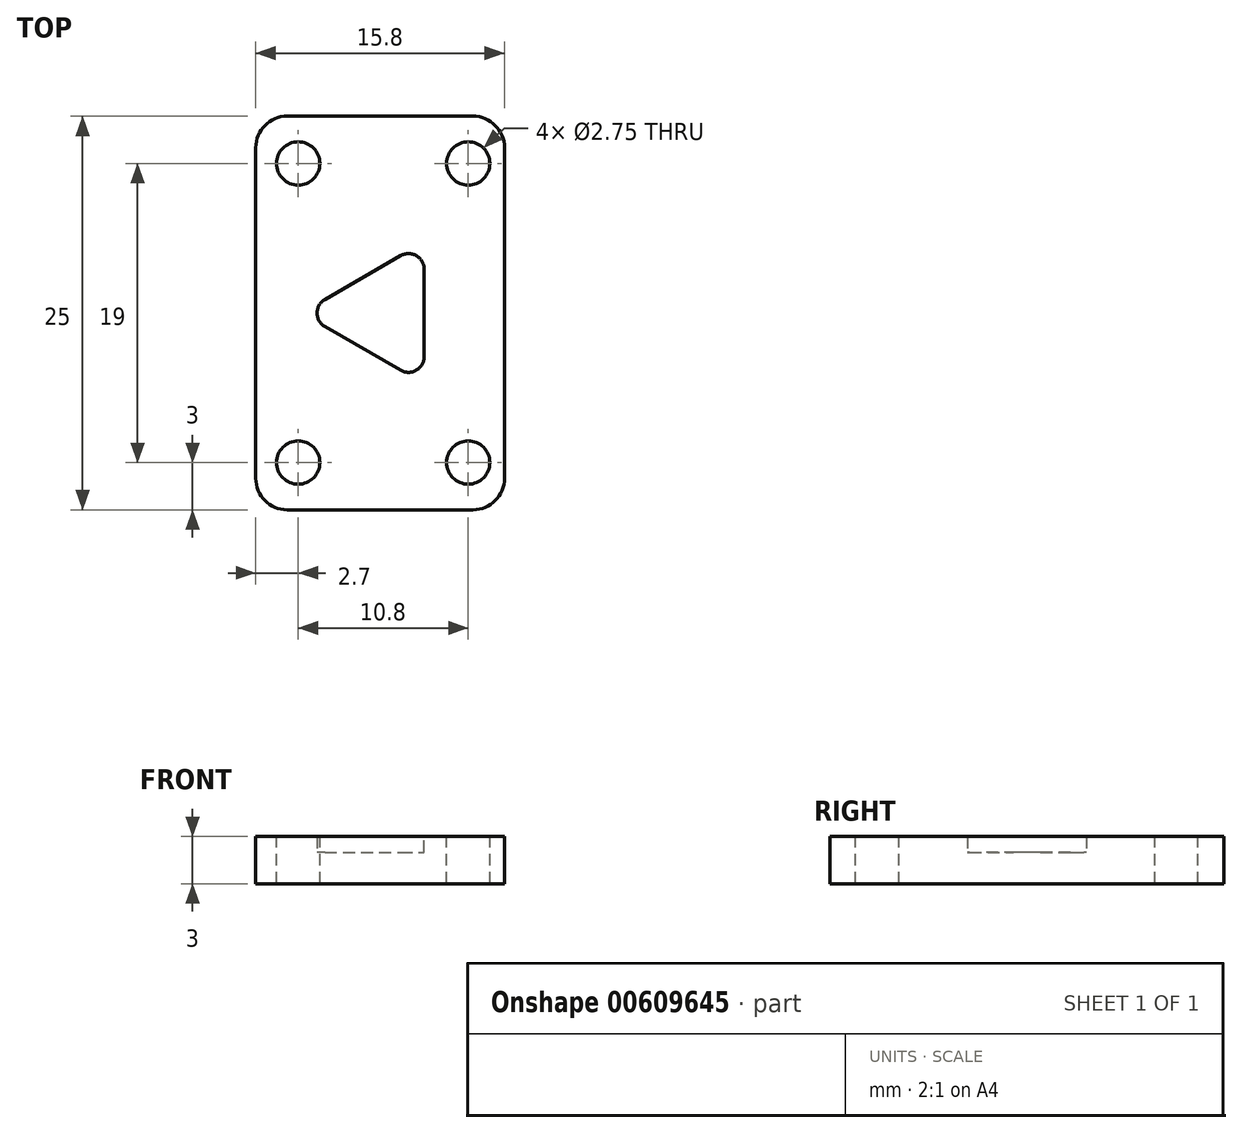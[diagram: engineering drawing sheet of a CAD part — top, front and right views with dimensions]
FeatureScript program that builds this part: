
annotation { "Feature Type Name" : "Feature", "Feature Type Description" : "" }
export const myFeature = defineFeature(function(context is Context, id is Id, definition is map)
    precondition{}
    {
        {
            var Q0;
            Q0=qCreatedBy(makeId("Top.planeOp"),FACE);
            var sketch = newSketch(context, id + "F0", { "sketchPlane" : qUnion([Q0])});
            skLineSegment(sketch, "E0.bottom", {"start": v(0, 0) * mm, "end": v(15.8, 0) * mm});
            skLineSegment(sketch, "E0.top", {"start": v(0, 25) * mm, "end": v(15.8, 25) * mm});
            skLineSegment(sketch, "E0.left", {"start": v(0, 0) * mm, "end": v(0, 25) * mm});
            skLineSegment(sketch, "E0.right", {"start": v(15.8, 0) * mm, "end": v(15.8, 25) * mm});
            skSolve(sketch);
        }
        {
            var Q0;
            Q0=makeQuery(id+"F0.imprint","IMPRINT",FACE,{"disambiguationData":[TD([[makeQuery(id+"F0.imprint","IMPRINT",EDGE,{"derivedFrom":sQuery(id+"F0.wireOp",EDGE,"E0.bottom")}),1.0]])]});
            extrude(context, id + "F1", {"entities" : qUnion([Q0]), "depth" : 3 * mm, "offsetDistance" : 25 * mm});
        }
        {
            var Q0;
            Q0=makeQuery(id+"F1.opExtrude","CAP_FACE",FACE,{"disambiguationData":[OSD([sQuery(id+"F0.wireOp",EDGE,"E0.bottom"),sQuery(id+"F0.wireOp",EDGE,"E0.top"),sQuery(id+"F0.wireOp",EDGE,"E0.left"),sQuery(id+"F0.wireOp",EDGE,"E0.right")])],"isStart":false});
            var sketch = newSketch(context, id + "F2", { "sketchPlane" : qUnion([Q0])});
            skCircle(sketch, "E1", {"center": v(8.1, 12.5) * mm, "radius": 2.6 * mm});
            skPoint(sketch, "E1.centerSnap0", {"position": v(0.1, 12.5) * mm});
            skPoint(sketch, "E1.centerSnap1", {"position": v(8.1, 0) * mm});
            skSolve(sketch);
        }
        {
            var Q0;
            Q0=makeQuery(id+"F1.opExtrude","CAP_FACE",FACE,{"disambiguationData":[OSD([sQuery(id+"F0.wireOp",EDGE,"E0.bottom"),sQuery(id+"F0.wireOp",EDGE,"E0.top"),sQuery(id+"F0.wireOp",EDGE,"E0.left"),sQuery(id+"F0.wireOp",EDGE,"E0.right")])],"isStart":false});
            var sketch = newSketch(context, id + "F3", { "sketchPlane" : qUnion([Q0])});
            skCircle(sketch, "E2", {"center": v(13.5, 3) * mm, "radius": 1.38 * mm});
            skSolve(sketch);
        }
        {
            var Q0;
            Q0=makeQuery(id+"F3.imprint","IMPRINT",FACE,{"disambiguationData":[TD([[makeQuery(id+"F3.imprint","IMPRINT",EDGE,{"derivedFrom":sQuery(id+"F3.wireOp",EDGE,"E2")}),-1.0]])]});
            var sketch = newSketch(context, id + "F4", { "sketchPlane" : qUnion([Q0])});
            skCircle(sketch, "E3", {"center": v(2.7, 3) * mm, "radius": 1.38 * mm});
            skSolve(sketch);
        }
        {
            var Q0;
            Q0=makeQuery(id+"F3.imprint","IMPRINT",FACE,{"disambiguationData":[TD([[makeQuery(id+"F3.imprint","IMPRINT",EDGE,{"derivedFrom":sQuery(id+"F3.wireOp",EDGE,"E2")}),-1.0]])]});
            var sketch = newSketch(context, id + "F5", { "sketchPlane" : qUnion([Q0])});
            skCircle(sketch, "E4", {"center": v(2.7, 22) * mm, "radius": 1.38 * mm});
            skSolve(sketch);
        }
        {
            var Q0;
            Q0=makeQuery(id+"F3.imprint","IMPRINT",FACE,{"disambiguationData":[TD([[makeQuery(id+"F3.imprint","IMPRINT",EDGE,{"derivedFrom":sQuery(id+"F3.wireOp",EDGE,"E2")}),-1.0]])]});
            var sketch = newSketch(context, id + "F6", { "sketchPlane" : qUnion([Q0])});
            skCircle(sketch, "E5", {"center": v(13.5, 22) * mm, "radius": 1.38 * mm});
            skSolve(sketch);
        }
        {
            var Q0;
            Q0=makeQuery(id+"F3.imprint","IMPRINT",FACE,{"disambiguationData":[TD([[makeQuery(id+"F3.imprint","IMPRINT",EDGE,{"derivedFrom":sQuery(id+"F3.wireOp",EDGE,"E2")}),1.0]])]});
            var Q1;
            Q1=makeQuery(id+"F4.imprint","IMPRINT",FACE,{"disambiguationData":[TD([[makeQuery(id+"F4.imprint","IMPRINT",EDGE,{"derivedFrom":sQuery(id+"F4.wireOp",EDGE,"E3")}),1.0]])]});
            extrude(context, id + "F7", {"entities" : qUnion([Q0, Q1]), "operationType" : NewBodyOperationType.REMOVE, "oppositeDirection" : true, "depth" : 5 * mm, "offsetDistance" : 25 * mm});
        }
        {
            var Q0;
            Q0=makeQuery(id+"F5.imprint","IMPRINT",FACE,{"disambiguationData":[TD([[makeQuery(id+"F5.imprint","IMPRINT",EDGE,{"derivedFrom":sQuery(id+"F5.wireOp",EDGE,"E4")}),1.0]])]});
            extrude(context, id + "F8", {"entities" : qUnion([Q0]), "operationType" : NewBodyOperationType.REMOVE, "oppositeDirection" : true, "depth" : 5 * mm, "offsetDistance" : 25 * mm});
        }
        {
            var Q0;
            Q0=makeQuery(id+"F6.imprint","IMPRINT",FACE,{"disambiguationData":[TD([[makeQuery(id+"F6.imprint","IMPRINT",EDGE,{"derivedFrom":sQuery(id+"F6.wireOp",EDGE,"E5")}),1.0]])]});
            extrude(context, id + "F9", {"entities" : qUnion([Q0]), "operationType" : NewBodyOperationType.REMOVE, "oppositeDirection" : true, "depth" : 5 * mm, "offsetDistance" : 25 * mm});
        }
        {
            var Q0;
            Q0=makeQuery(id+"F1.opExtrude","SWEPT_EDGE",EDGE,{"disambiguationData":[OSD([sQuery(id+"F0.wireOp",EDGE,"E0.top"),sQuery(id+"F0.wireOp",EDGE,"E0.right")])]});
            var Q1;
            Q1=makeQuery(id+"F1.opExtrude","SWEPT_EDGE",EDGE,{"disambiguationData":[OSD([sQuery(id+"F0.wireOp",EDGE,"E0.bottom"),sQuery(id+"F0.wireOp",EDGE,"E0.right")])]});
            var Q2;
            Q2=makeQuery(id+"F1.opExtrude","SWEPT_EDGE",EDGE,{"disambiguationData":[OSD([sQuery(id+"F0.wireOp",EDGE,"E0.bottom"),sQuery(id+"F0.wireOp",EDGE,"E0.left")])]});
            var Q3;
            Q3=makeQuery(id+"F1.opExtrude","SWEPT_EDGE",EDGE,{"disambiguationData":[OSD([sQuery(id+"F0.wireOp",EDGE,"E0.top"),sQuery(id+"F0.wireOp",EDGE,"E0.left")])]});
            fillet(context, id + "F10", {"entities" : qUnion([Q0, Q1, Q2, Q3]), "radius" : 2 * mm, "tangentPropagation" : true, "allowEdgeOverflow" : false});
        }
        {
            var Q0;
            Q0=makeQuery(id+"F2.imprint","IMPRINT",FACE,{"disambiguationData":[TD([[makeQuery(id+"F2.imprint","IMPRINT",EDGE,{"derivedFrom":sQuery(id+"F2.wireOp",EDGE,"E1")}),1.0]])]});
            var sketch = newSketch(context, id + "F11", { "sketchPlane" : qUnion([Q0])});
            skCircle(sketch, "E6.cCircle", {"center": v(8.1, 12.5) * mm, "radius": 2.6 * mm, "construction": true});
            skLineSegment(sketch, "E6.0", {"start": v(2.9, 12.5) * mm, "end": v(10.7, 17) * mm});
            skLineSegment(sketch, "E6.1", {"start": v(10.7, 17) * mm, "end": v(10.7, 8) * mm});
            skLineSegment(sketch, "E6.2", {"start": v(10.7, 8) * mm, "end": v(2.9, 12.5) * mm});
            skPoint(sketch, "E6.0.midPoint", {"position": v(6.8, 14.75) * mm});
            skSolve(sketch);
        }
        {
            var Q0;
            Q0 = qSketchRegion(id + "F11", true);
            extrude(context, id + "F12", {"entities" : qUnion([Q0]), "operationType" : NewBodyOperationType.REMOVE, "oppositeDirection" : true, "depth" : 1 * mm, "offsetDistance" : 25 * mm});
        }
        {
            var Q0;
            Q0=makeQuery(id+"F12.boolean.opBoolean","COPY",EDGE,{"derivedFrom":makeQuery(id+"F12.opExtrude","SWEPT_EDGE",EDGE,{"disambiguationData":[OSD([sQuery(id+"F11.wireOp",EDGE,"E6.0"),sQuery(id+"F11.wireOp",EDGE,"E6.2")])]})});
            var Q1;
            Q1=makeQuery(id+"F12.boolean.opBoolean","COPY",EDGE,{"derivedFrom":makeQuery(id+"F12.opExtrude","SWEPT_EDGE",EDGE,{"disambiguationData":[OSD([sQuery(id+"F11.wireOp",EDGE,"E6.0"),sQuery(id+"F11.wireOp",EDGE,"E6.1")])]})});
            var Q2;
            Q2=makeQuery(id+"F12.boolean.opBoolean","COPY",EDGE,{"derivedFrom":makeQuery(id+"F12.opExtrude","SWEPT_EDGE",EDGE,{"disambiguationData":[OSD([sQuery(id+"F11.wireOp",EDGE,"E6.1"),sQuery(id+"F11.wireOp",EDGE,"E6.2")])]})});
            fillet(context, id + "F13", {"entities" : qUnion([Q0, Q1, Q2]), "radius" : 1 * mm, "tangentPropagation" : true, "allowEdgeOverflow" : false});
        }
    });
